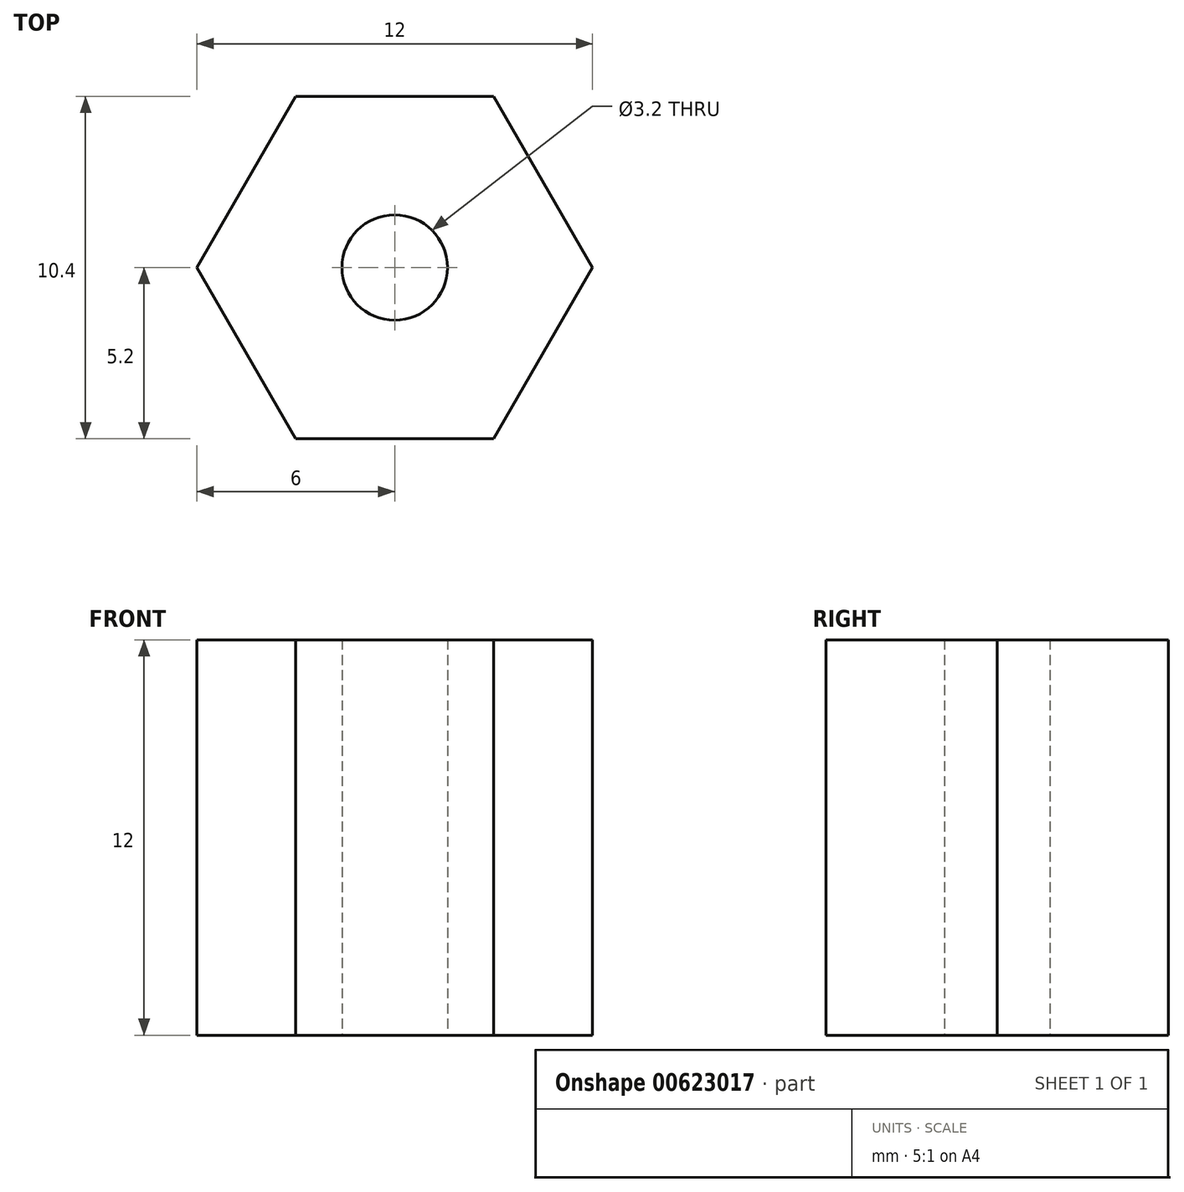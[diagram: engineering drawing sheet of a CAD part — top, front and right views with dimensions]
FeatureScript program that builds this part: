
annotation { "Feature Type Name" : "Feature", "Feature Type Description" : "" }
export const myFeature = defineFeature(function(context is Context, id is Id, definition is map)
    precondition{}
    {
        {
            var Q0;
            Q0=qCreatedBy(makeId("Top.planeOp"),FACE);
            var sketch = newSketch(context, id + "F0", { "sketchPlane" : qUnion([Q0])});
            skCircle(sketch, "E0.cCircle", {"center": v(0, 0) * mm, "radius": 6 * mm, "construction": true});
            skLineSegment(sketch, "E0.0", {"start": v(6, 0) * mm, "end": v(3, -5.2) * mm});
            skLineSegment(sketch, "E0.1", {"start": v(3, -5.2) * mm, "end": v(-3, -5.2) * mm});
            skLineSegment(sketch, "E0.2", {"start": v(-3, -5.2) * mm, "end": v(-6, 0) * mm});
            skLineSegment(sketch, "E0.3", {"start": v(-6, 0) * mm, "end": v(-3, 5.2) * mm});
            skLineSegment(sketch, "E0.4", {"start": v(-3, 5.2) * mm, "end": v(3, 5.2) * mm});
            skLineSegment(sketch, "E0.5", {"start": v(3, 5.2) * mm, "end": v(6, 0) * mm});
            skCircle(sketch, "E1", {"center": v(0, 0) * mm, "radius": 1.6 * mm});
            skSolve(sketch);
        }
        {
            var Q0;
            Q0 = qSketchRegion(id + "F0", true);
            extrude(context, id + "F1", {"entities" : qUnion([Q0]), "depth" : 12 * mm, "offsetDistance" : 25 * mm});
        }
    });
